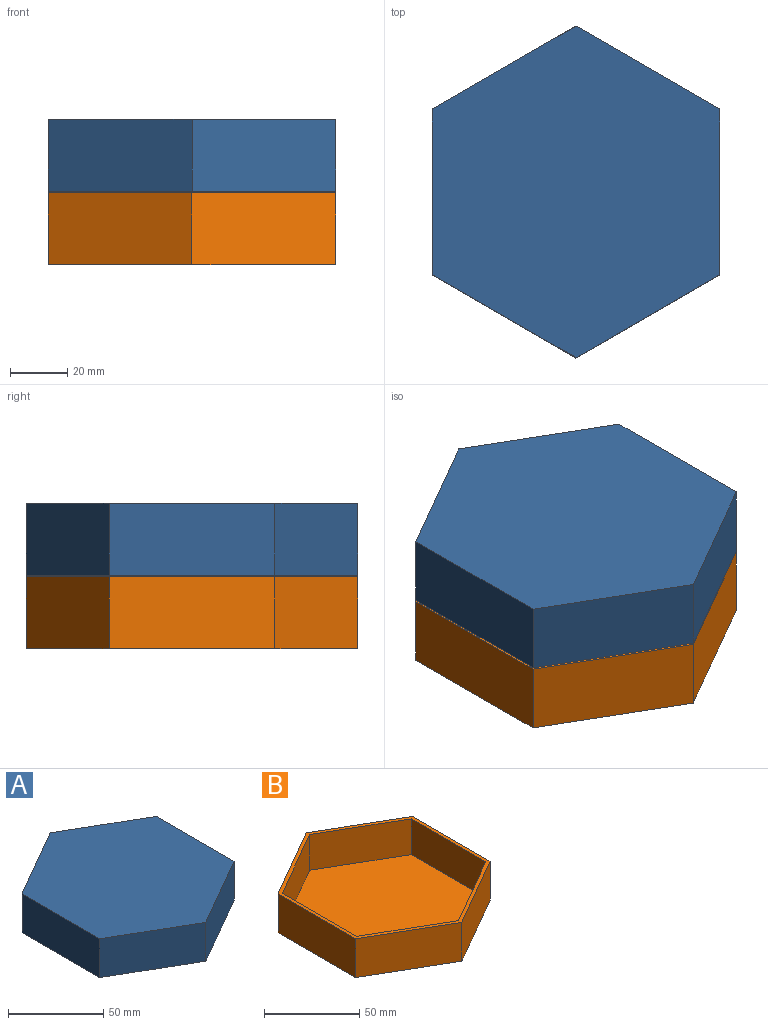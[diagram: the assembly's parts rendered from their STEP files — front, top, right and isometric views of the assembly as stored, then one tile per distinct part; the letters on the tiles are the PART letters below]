
ASSEMBLY  parts=2 mates=1
PART A: 15 faces, bbox 100x115.5x25 mm
  f0: plane 50x28.87mm, normal (-0.5,-0.87,0), area 1443.4mm2, adj f1,f5,f6,f13
  f1: plane 57.74x25mm, normal (-1,0,0), area 1443.4mm2, adj f0,f2,f6,f13
  f2: plane 50x28.87mm, normal (-0.5,0.87,0), area 1443.4mm2, adj f1,f3,f6,f13
  f3: plane 50x28.87mm, normal (0.5,0.87,0), area 1443.4mm2, adj f2,f4,f6,f13
  f4: plane 57.74x25mm, normal (1,0,0), area 1443.4mm2, adj f3,f5,f6,f13
  f5: plane 50x28.87mm, normal (0.5,-0.87,0), area 1443.4mm2, adj f0,f4,f6,f13
  f6: plane 115.47x100mm, normal (0,0,1), area 8660.3mm2, adj f0,f1,f2,f3,f4,f5
  f7: plane 55.43x23mm, normal (1,0,0), area 1274.8mm2, adj f8,f12,f13,f14
  f8: plane 48x27.71mm, normal (0.5,0.87,0), area 1274.8mm2, adj f7,f9,f13,f14
  f9: plane 48x27.71mm, normal (-0.5,0.87,0), area 1274.8mm2, adj f8,f10,f13,f14
  f10: plane 55.43x23mm, normal (-1,0,0), area 1274.8mm2, adj f9,f11,f13,f14
  f11: plane 48x27.71mm, normal (-0.5,-0.87,0), area 1274.8mm2, adj f10,f12,f13,f14
  f12: plane 48x27.71mm, normal (0.5,-0.87,0), area 1274.8mm2, adj f7,f11,f13,f14
  f13: plane 115.47x100mm, normal (0,0,-1), area 679mm2, adj f0,f1,f2,f3,f4,f5,f7,f8
  f14: plane 110.85x96mm, normal (0,0,-1), area 7981.3mm2, adj f7,f8,f9,f10,f11,f12
PART B: 15 faces, bbox 100x115.5x25 mm
  f0: plane 57.74x25mm, normal (-1,0,0), area 1443.4mm2, adj f1,f5,f6,f13
  f1: plane 50x28.87mm, normal (-0.5,-0.87,0), area 1443.4mm2, adj f0,f2,f6,f13
  f2: plane 50x28.87mm, normal (0.5,-0.87,0), area 1443.4mm2, adj f1,f3,f6,f13
  f3: plane 57.74x25mm, normal (1,0,0), area 1443.4mm2, adj f2,f4,f6,f13
  f4: plane 50x28.87mm, normal (0.5,0.87,0), area 1443.4mm2, adj f3,f5,f6,f13
  f5: plane 50x28.87mm, normal (-0.5,0.87,0), area 1443.4mm2, adj f0,f4,f6,f13
  f6: plane 115.47x100mm, normal (0,0,-1), area 8660.3mm2, adj f0,f1,f2,f3,f4,f5
  f7: plane 48x27.71mm, normal (0.5,0.87,0), area 1274.8mm2, adj f8,f12,f13,f14
  f8: plane 55.43x23mm, normal (1,0,0), area 1274.8mm2, adj f7,f9,f13,f14
  f9: plane 48x27.71mm, normal (0.5,-0.87,0), area 1274.8mm2, adj f8,f10,f13,f14
  f10: plane 48x27.71mm, normal (-0.5,-0.87,0), area 1274.8mm2, adj f9,f11,f13,f14
  f11: plane 55.43x23mm, normal (-1,0,0), area 1274.8mm2, adj f10,f12,f13,f14
  f12: plane 48x27.71mm, normal (-0.5,0.87,0), area 1274.8mm2, adj f7,f11,f13,f14
  f13: plane 115.47x100mm, normal (0,0,1), area 679mm2, adj f0,f1,f2,f3,f4,f5,f7,f8
  f14: plane 110.85x96mm, normal (0,0,1), area 7981.3mm2, adj f7,f8,f9,f10,f11,f12
PLACE A t=(47.11,55.71,-42.72)mm
PLACE B t=(-0.95,138.85,-89.24)mm
MATE parallel A.f0 <-> B.f1  axis (-0.5,-0.87,0) through (-25.89,95.55,-51.22)mm
